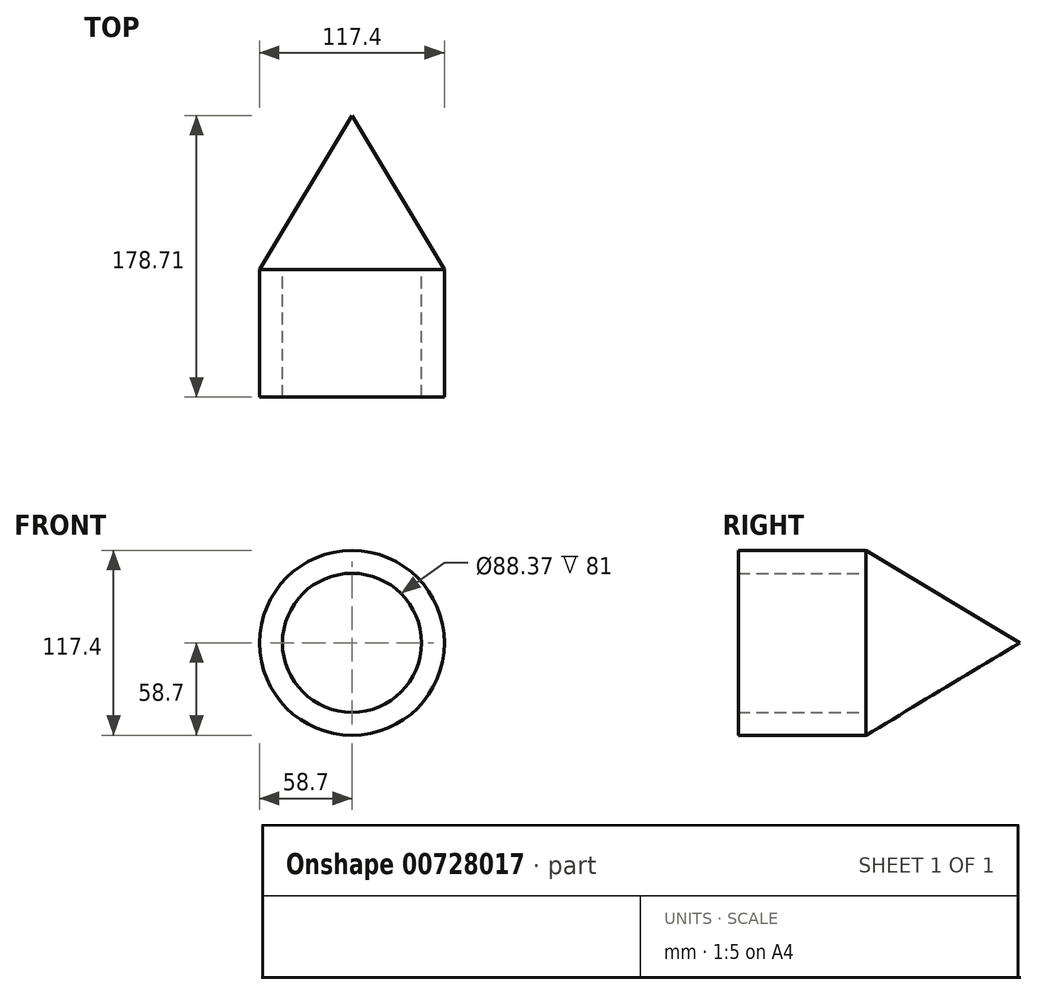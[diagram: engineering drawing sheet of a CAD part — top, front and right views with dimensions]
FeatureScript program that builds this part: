
annotation { "Feature Type Name" : "Feature", "Feature Type Description" : "" }
export const myFeature = defineFeature(function(context is Context, id is Id, definition is map)
    precondition{}
    {
        {
            var Q0;
            Q0=qCreatedBy(makeId("Front.planeOp"),FACE);
            var sketch = newSketch(context, id + "F0", { "sketchPlane" : qUnion([Q0])});
            skCircle(sketch, "E0", {"center": v(0, 0) * mm, "radius": 58.7 * mm});
            skCircle(sketch, "E1", {"center": v(0, 0) * mm, "radius": 44.18 * mm});
            skSolve(sketch);
        }
        {
            var Q0;
            Q0=makeQuery(id+"F0.imprint","IMPRINT",FACE,{"disambiguationData":[TD([[makeQuery(id+"F0.imprint","IMPRINT",EDGE,{"derivedFrom":sQuery(id+"F0.wireOp",EDGE,"E0")}),1.0]])]});
            extrude(context, id + "F1", {"entities" : qUnion([Q0]), "depth" : 81 * mm, "offsetDistance" : 25 * mm});
        }
        {
            var Q0;
            Q0=qCreatedBy(makeId("Right.planeOp"),FACE);
            var sketch = newSketch(context, id + "F2", { "sketchPlane" : qUnion([Q0])});
            skLineSegment(sketch, "E2", {"start": v(0, 0) * mm, "end": v(97.71, 0) * mm});
            skLineSegment(sketch, "E3", {"start": v(97.71, 0) * mm, "end": v(0, -58.67) * mm});
            skLineSegment(sketch, "E4", {"start": v(0, -58.67) * mm, "end": v(0, 0) * mm});
            skSolve(sketch);
        }
        {
            var Q0;
            Q0=qCreatedBy(makeId("Right.planeOp"),FACE);
            var sketch = newSketch(context, id + "F3", { "sketchPlane" : qUnion([Q0])});
            skLineSegment(sketch, "E5", {"start": v(0, 0) * mm, "end": v(82.43, 0) * mm});
            skLineSegment(sketch, "E6", {"start": v(0, -57.75) * mm, "end": v(82.43, 0) * mm});
            skLineSegment(sketch, "E7", {"start": v(0, 2.61) * mm, "end": v(0, -57.75) * mm});
            skSolve(sketch);
        }
        {
            var Q0;
            Q0=makeQuery(id+"F2.imprint","IMPRINT",FACE,{"disambiguationData":[TD([[makeQuery(id+"F2.imprint","IMPRINT",EDGE,{"derivedFrom":sQuery(id+"F2.wireOp",EDGE,"E2")}),-1.0]])]});
            var Q1;
            Q1=sQuery(id+"F3.wireOp",EDGE,"E5");
            revolve(context, id + "F4", {"operationType" : NewBodyOperationType.ADD, "surfaceOperationType" : NewSurfaceOperationType.NEW, "entities" : qUnion([Q0]), "axis" : qUnion([Q1]), "revolveType" : RevolveType.FULL});
        }
    });
